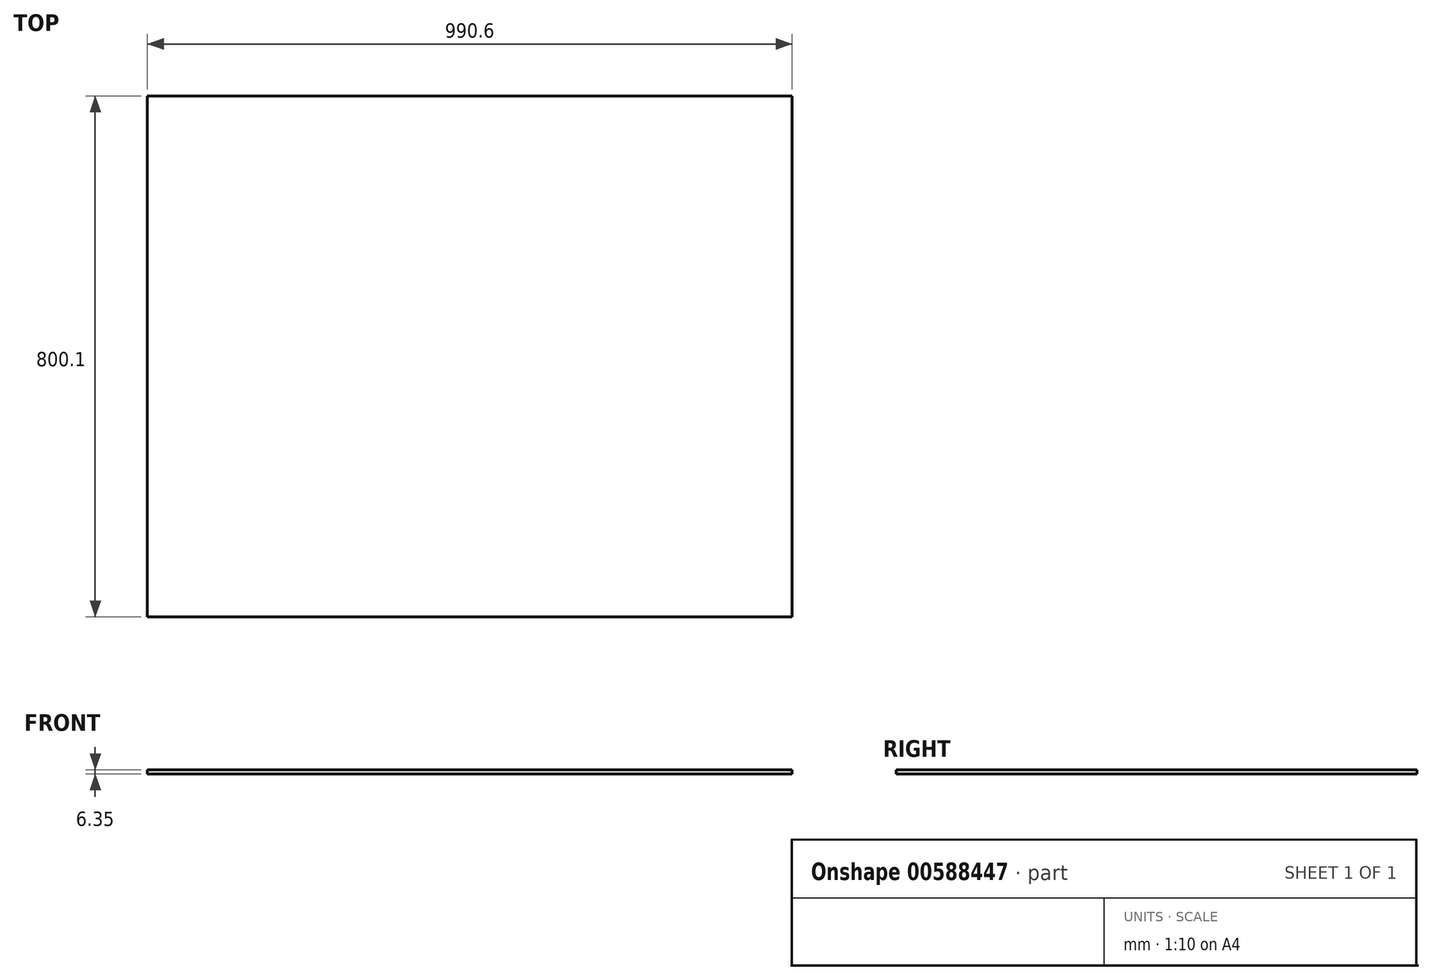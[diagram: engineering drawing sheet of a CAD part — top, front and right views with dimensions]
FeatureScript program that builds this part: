
annotation { "Feature Type Name" : "Feature", "Feature Type Description" : "" }
export const myFeature = defineFeature(function(context is Context, id is Id, definition is map)
    precondition{}
    {
        {
            var Q0;
            Q0=qCreatedBy(makeId("Top.planeOp"),FACE);
            var sketch = newSketch(context, id + "F0", { "sketchPlane" : qUnion([Q0])});
            skLineSegment(sketch, "E0.bottom", {"start": v(0, 0) * mm, "end": v(990.6, 0) * mm});
            skLineSegment(sketch, "E0.top", {"start": v(0, 800.1) * mm, "end": v(990.6, 800.1) * mm});
            skLineSegment(sketch, "E0.left", {"start": v(0, 0) * mm, "end": v(0, 800.1) * mm});
            skLineSegment(sketch, "E0.right", {"start": v(990.6, 0) * mm, "end": v(990.6, 800.1) * mm});
            skSolve(sketch);
        }
        {
            var Q0;
            Q0 = qSketchRegion(id + "F0", true);
            extrude(context, id + "F1", {"entities" : qUnion([Q0]), "oppositeDirection" : true, "depth" : 6.35 * mm, "offsetDistance" : 25.4 * mm});
        }
    });
